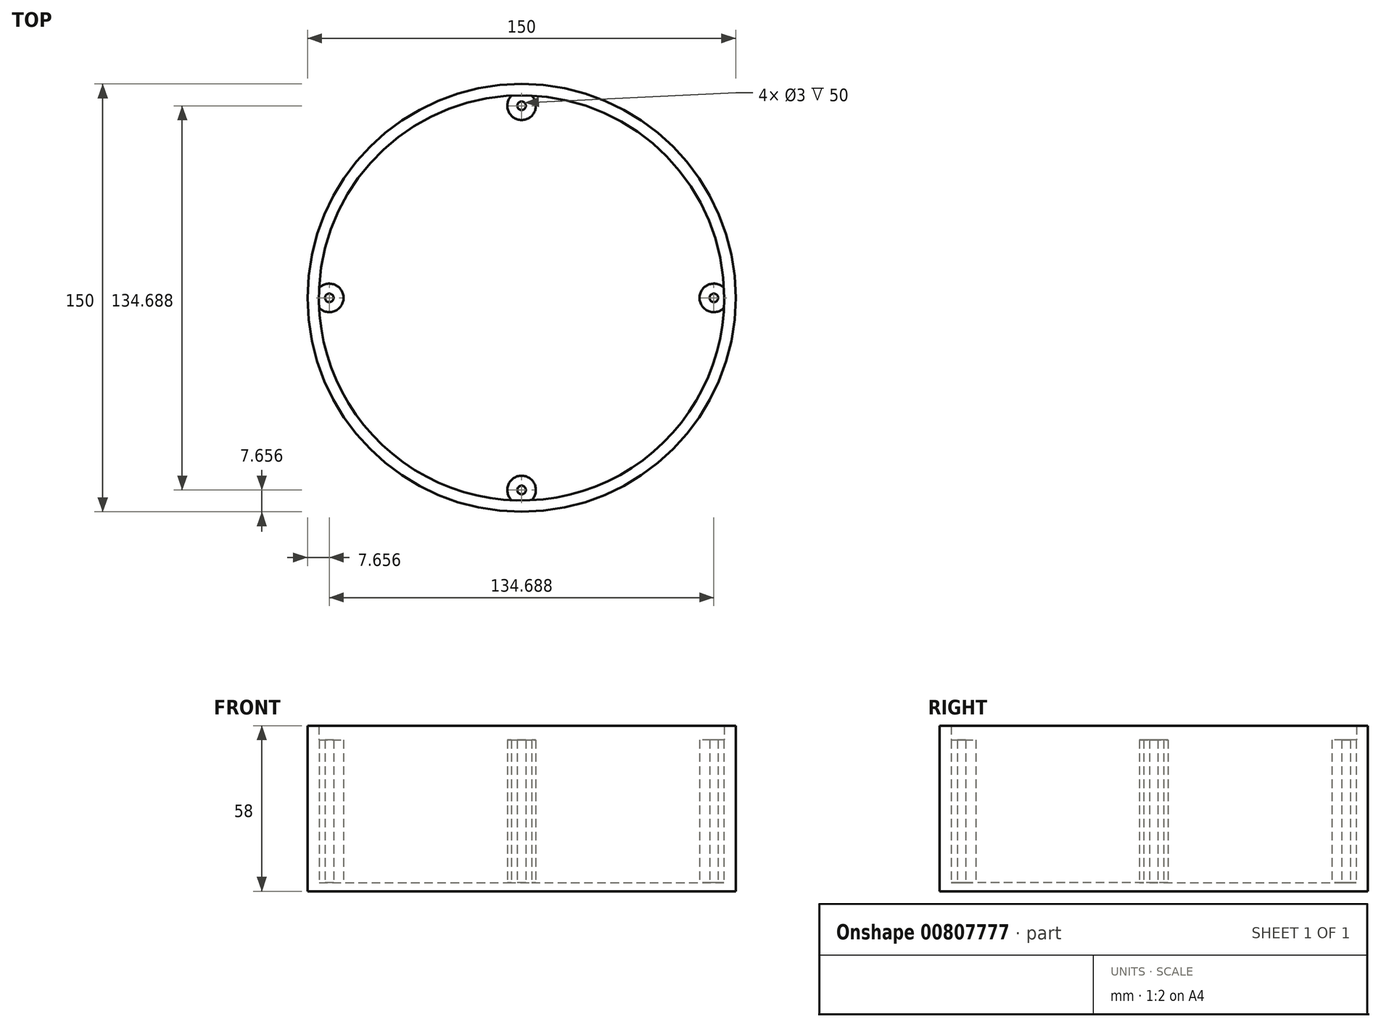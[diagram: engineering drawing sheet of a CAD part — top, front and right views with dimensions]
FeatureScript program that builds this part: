
annotation { "Feature Type Name" : "Feature", "Feature Type Description" : "" }
export const myFeature = defineFeature(function(context is Context, id is Id, definition is map)
    precondition{}
    {
        {
            var Q0;
            Q0=qCreatedBy(makeId("Top.planeOp"),FACE);
            var sketch = newSketch(context, id + "F0", { "sketchPlane" : qUnion([Q0])});
            skCircle(sketch, "E0", {"center": v(0, 0) * mm, "radius": 75 * mm});
            skSolve(sketch);
        }
        {
            var Q0;
            Q0 = qSketchRegion(id + "F0", true);
            extrude(context, id + "F1", {"entities" : qUnion([Q0]), "depth" : 3 * mm, "offsetDistance" : 25 * mm});
        }
        {
            var Q0;
            Q0=makeQuery(id+"F1.opExtrude","CAP_FACE",FACE,{"disambiguationData":[OSD([sQuery(id+"F0.wireOp",EDGE,"E0")])],"isStart":false});
            var sketch = newSketch(context, id + "F2", { "sketchPlane" : qUnion([Q0])});
            skCircle(sketch, "E1.0", {"center": v(0, 0) * mm, "radius": 71 * mm});
            skCircle(sketch, "E2.0", {"center": v(0, 0) * mm, "radius": 75 * mm});
            skSolve(sketch);
        }
        {
            var Q0;
            Q0 = qSketchRegion(id + "F2", true);
            extrude(context, id + "F3", {"entities" : qUnion([Q0]), "operationType" : NewBodyOperationType.ADD, "depth" : 55 * mm, "offsetDistance" : 25 * mm});
        }
        {
            var Q0;
            Q0=makeQuery(id+"F1.opExtrude","CAP_FACE",FACE,{"disambiguationData":[OSD([sQuery(id+"F0.wireOp",EDGE,"E0")])],"isStart":false});
            var sketch = newSketch(context, id + "F4", { "sketchPlane" : qUnion([Q0])});
            skCircle(sketch, "E3", {"center": v(0, 67.34) * mm, "radius": 5 * mm});
            skCircle(sketch, "E4", {"center": v(0, 67.34) * mm, "radius": 1.5 * mm});
            skCircle(sketch, "E5.1.0", {"center": v(-67.34, 0) * mm, "radius": 5 * mm});
            skCircle(sketch, "E5.1.1", {"center": v(-67.34, 0) * mm, "radius": 1.5 * mm});
            skCircle(sketch, "E5.2.0", {"center": v(0, -67.34) * mm, "radius": 5 * mm});
            skCircle(sketch, "E5.2.1", {"center": v(0, -67.34) * mm, "radius": 1.5 * mm});
            skCircle(sketch, "E5.3.0", {"center": v(67.34, 0) * mm, "radius": 5 * mm});
            skCircle(sketch, "E5.3.1", {"center": v(67.34, 0) * mm, "radius": 1.5 * mm});
            skPoint(sketch, "E5.center", {"position": v(0, 0) * mm});
            skSolve(sketch);
        }
        {
            var Q0;
            Q0 = qSketchRegion(id + "F4", true);
            extrude(context, id + "F5", {"entities" : qUnion([Q0]), "operationType" : NewBodyOperationType.ADD, "depth" : 50 * mm, "offsetDistance" : 25 * mm});
        }
    });
